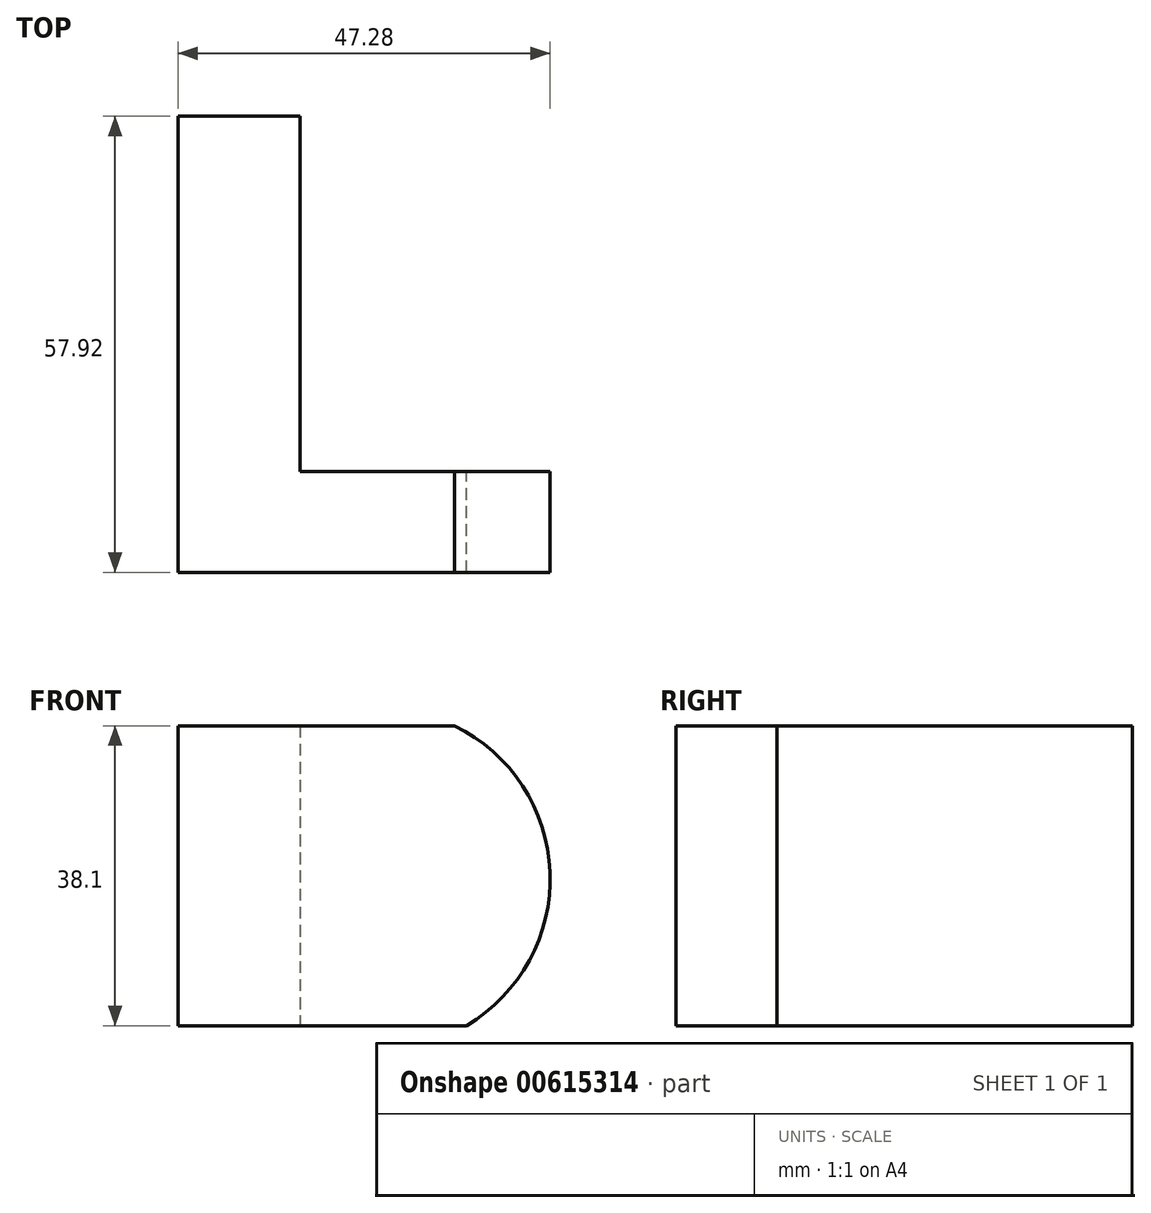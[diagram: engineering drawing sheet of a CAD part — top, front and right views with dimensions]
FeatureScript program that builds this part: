
annotation { "Feature Type Name" : "Feature", "Feature Type Description" : "" }
export const myFeature = defineFeature(function(context is Context, id is Id, definition is map)
    precondition{}
    {
        {
            var Q0;
            Q0=qCreatedBy(makeId("Top.planeOp"),FACE);
            var sketch = newSketch(context, id + "F0", { "sketchPlane" : qUnion([Q0])});
            skLineSegment(sketch, "E0", {"start": v(0, 0) * mm, "end": v(0, 57.92) * mm});
            skLineSegment(sketch, "E1", {"start": v(0, 57.92) * mm, "end": v(15.47, 57.92) * mm});
            skLineSegment(sketch, "E2", {"start": v(15.47, 57.92) * mm, "end": v(15.47, 12.78) * mm});
            skLineSegment(sketch, "E3", {"start": v(15.47, 12.78) * mm, "end": v(47.28, 12.78) * mm});
            skLineSegment(sketch, "E4", {"start": v(47.28, 12.78) * mm, "end": v(47.28, 0) * mm});
            skLineSegment(sketch, "E5", {"start": v(47.28, 0) * mm, "end": v(0, 0) * mm});
            skSolve(sketch);
        }
        {
            var Q0;
            Q0 = qSketchRegion(id + "F0", true);
            extrude(context, id + "F1", {"entities" : qUnion([Q0]), "depth" : 38.1 * mm, "offsetDistance" : 25.4 * mm});
        }
        {
            var Q0;
            Q0=makeQuery(id+"F1.opExtrude","SWEPT_FACE",FACE,{"disambiguationData":[OSD([sQuery(id+"F0.wireOp",EDGE,"E3")])]});
            var sketch = newSketch(context, id + "F2", { "sketchPlane" : qUnion([Q0])});
            skArc(sketch, "E6", {"start": v(-35.12, 38.1) * mm, "mid": v(-47.26, 19.5) * mm, "end": v(-36.63, 0) * mm});
            skSolve(sketch);
        }
        {
            var Q0;
            {var subQ0=sQuery(id+"F2.wireOp",EDGE,"E6");var subQ1=sQuery(id+"F0.wireOp",EDGE,"E3");var subQ2=makeQuery(id+"F1.opExtrude","CAP_EDGE",EDGE,{"disambiguationData":[OSD([subQ1])],"isStart":false});var subQ3=makeQuery(id+"F2.imprint","INTERSECT",VERTEX,{"derivedFrom":[subQ2,subQ0]});Q0=makeQuery(id+"F2.imprint","IMPRINT",FACE,{"disambiguationData":[TD([[makeQuery(id+"F2.imprint","IMPRINT",EDGE,{"disambiguationData":[TD([[subQ3,-1.0]])],"derivedFrom":subQ0}),-1.0]])]});}
            var Q1;
            {var subQ0=sQuery(id+"F2.wireOp",EDGE,"E6");var subQ1=sQuery(id+"F0.wireOp",EDGE,"E3");var subQ2=makeQuery(id+"F1.opExtrude","CAP_EDGE",EDGE,{"disambiguationData":[OSD([subQ1])],"isStart":true});var subQ3=makeQuery(id+"F2.imprint","INTERSECT",VERTEX,{"derivedFrom":[subQ2,subQ0]});Q1=makeQuery(id+"F2.imprint","IMPRINT",FACE,{"disambiguationData":[TD([[makeQuery(id+"F2.imprint","IMPRINT",EDGE,{"disambiguationData":[TD([[subQ3,1.0]])],"derivedFrom":subQ0}),-1.0]])]});}
            extrude(context, id + "F3", {"entities" : qUnion([Q0, Q1]), "operationType" : NewBodyOperationType.REMOVE, "endBound" : BoundingType.THROUGH_ALL, "oppositeDirection" : true, "depth" : 25.4 * mm, "offsetDistance" : 25.4 * mm});
        }
    });
